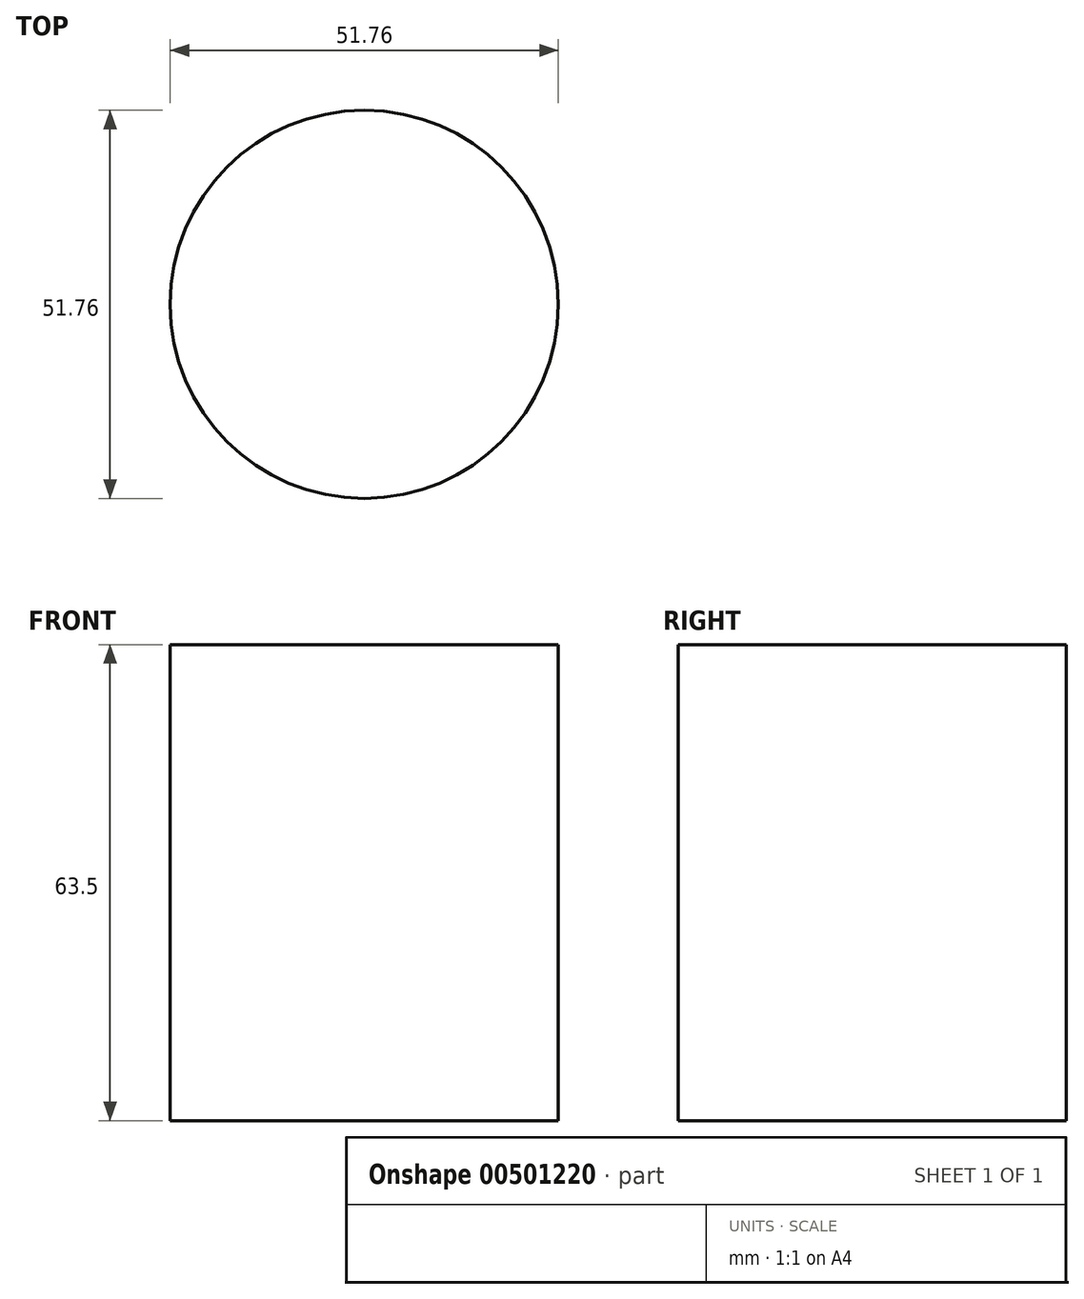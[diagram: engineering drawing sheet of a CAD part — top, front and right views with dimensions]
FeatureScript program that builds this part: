
annotation { "Feature Type Name" : "Feature", "Feature Type Description" : "" }
export const myFeature = defineFeature(function(context is Context, id is Id, definition is map)
    precondition{}
    {
        {
            var Q0;
            Q0=qCreatedBy(makeId("Top.planeOp"),FACE);
            var sketch = newSketch(context, id + "F0", { "sketchPlane" : qUnion([Q0])});
            skCircle(sketch, "E0", {"center": v(0, 0) * mm, "radius": 25.88 * mm});
            skSolve(sketch);
        }
        {
            var Q0;
            Q0 = qSketchRegion(id + "F0", true);
            extrude(context, id + "F1", {"entities" : qUnion([Q0]), "depth" : 63.5 * mm});
        }
    });
